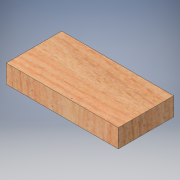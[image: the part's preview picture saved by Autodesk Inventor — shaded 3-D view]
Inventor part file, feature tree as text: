
AUTODESK INVENTOR PART (.ipt)
format: ipt  version: 2016 (Build 200138000, 138)  size: 128,000 bytes
history: native  units: in
note: dims shown in document units (in); Inventor stores cm internally (conversion verified against a paired STEP export)
features: extrude x1, sketch x1
ambient origin geometry x8: Origin, YZ Plane, XZ Plane, XY Plane, X Axis, Y Axis, Z Axis, Center Point
bodies: Solid1 (feature_tree)
feature tree (2):
  extrude  "Extrusion1"  Depth=3.0in
  sketch  "Sketch1"  dims[d0=6.07in d1=3.0in d2=1.0in d3=0.0in]
